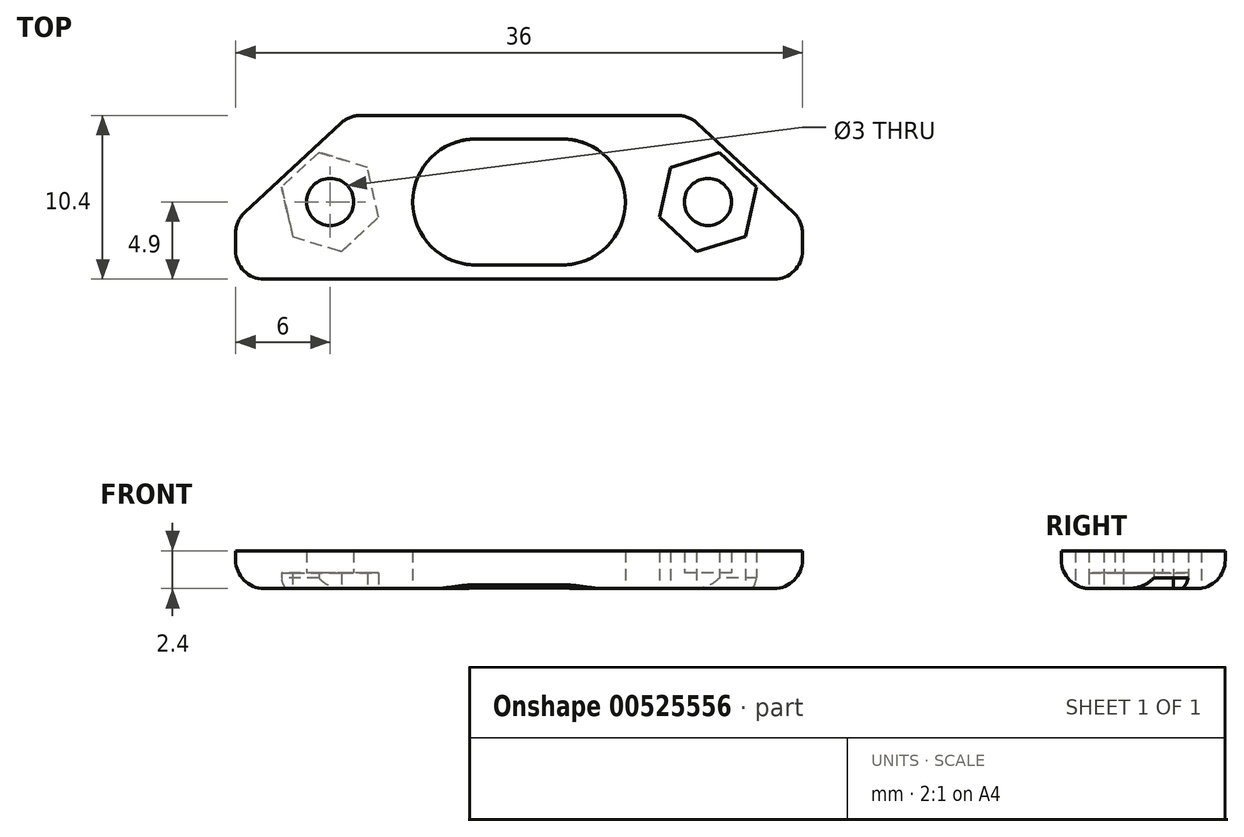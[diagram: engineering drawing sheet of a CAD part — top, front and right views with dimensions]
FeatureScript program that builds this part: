
annotation { "Feature Type Name" : "Feature", "Feature Type Description" : "" }
export const myFeature = defineFeature(function(context is Context, id is Id, definition is map)
    precondition{}
    {
        {
            var Q0;
            Q0=qCreatedBy(makeId("Top.planeOp"),FACE);
            var sketch = newSketch(context, id + "F0", { "sketchPlane" : qUnion([Q0])});
            skLineSegment(sketch, "E0.bottom", {"start": v(-18, -4.9) * mm, "end": v(18, -4.9) * mm});
            skLineSegment(sketch, "E0.top", {"start": v(-10.78, 5.5) * mm, "end": v(10.78, 5.5) * mm});
            skLineSegment(sketch, "E0.left", {"start": v(-18, -4.9) * mm, "end": v(-18, -1.2) * mm});
            skLineSegment(sketch, "E0.right", {"start": v(18, -4.9) * mm, "end": v(18, -1.2) * mm});
            skCircle(sketch, "E1", {"center": v(-12, 0) * mm, "radius": 1.5 * mm});
            skCircle(sketch, "E2.MirrorC", {"center": v(12, 0) * mm, "radius": 1.5 * mm});
            skArc(sketch, "E3", {"start": v(-2.75, 4) * mm, "mid": v(-6.75, 0) * mm, "end": v(-2.75, -4) * mm});
            skArc(sketch, "E4", {"start": v(2.75, -4) * mm, "mid": v(6.75, 0) * mm, "end": v(2.75, 4) * mm});
            skLineSegment(sketch, "E5", {"start": v(-2.75, 4) * mm, "end": v(2.75, 4) * mm});
            skLineSegment(sketch, "E6", {"start": v(-2.75, -4) * mm, "end": v(2.75, -4) * mm});
            skLineSegment(sketch, "E7", {"start": v(18, -1.2) * mm, "end": v(10.78, 5.5) * mm});
            skLineSegment(sketch, "E8.MirrorCS", {"start": v(-18, -1.2) * mm, "end": v(-10.78, 5.5) * mm});
            skPoint(sketch, "E9.center.orphan", {"position": v(-15.26, 6.06) * mm});
            skCircle(sketch, "E10.cCircle", {"center": v(12, 0) * mm, "radius": 2.8 * mm, "construction": true});
            skLineSegment(sketch, "E10.0", {"start": v(12.72, 3.15) * mm, "end": v(15.09, 0.95) * mm});
            skLineSegment(sketch, "E10.1", {"start": v(15.09, 0.95) * mm, "end": v(14.37, -2.2) * mm});
            skLineSegment(sketch, "E10.2", {"start": v(14.37, -2.2) * mm, "end": v(11.28, -3.15) * mm});
            skLineSegment(sketch, "E10.3", {"start": v(11.28, -3.15) * mm, "end": v(8.91, -0.95) * mm});
            skLineSegment(sketch, "E10.4", {"start": v(8.91, -0.95) * mm, "end": v(9.63, 2.2) * mm});
            skLineSegment(sketch, "E10.5", {"start": v(9.63, 2.2) * mm, "end": v(12.72, 3.15) * mm});
            skPoint(sketch, "E10.0.midPoint", {"position": v(13.9, 2.05) * mm});
            skLineSegment(sketch, "E11.MirrorCS", {"start": v(-8.91, -0.95) * mm, "end": v(-9.63, 2.2) * mm});
            skLineSegment(sketch, "E12.MirrorCS", {"start": v(-9.63, 2.2) * mm, "end": v(-12.72, 3.15) * mm});
            skLineSegment(sketch, "E13.MirrorCS", {"start": v(-12.72, 3.15) * mm, "end": v(-15.09, 0.95) * mm});
            skLineSegment(sketch, "E14.MirrorCS", {"start": v(-15.09, 0.95) * mm, "end": v(-14.37, -2.2) * mm});
            skLineSegment(sketch, "E15.MirrorCS", {"start": v(-14.37, -2.2) * mm, "end": v(-11.28, -3.15) * mm});
            skLineSegment(sketch, "E16.MirrorCS", {"start": v(-11.28, -3.15) * mm, "end": v(-8.91, -0.95) * mm});
            skCircle(sketch, "E17.MirrorC", {"center": v(-12, 0) * mm, "radius": 2.8 * mm, "construction": true});
            skSolve(sketch);
        }
        {
            var Q0;
            Q0=qSketchRegion(id+"F0",true);
            var Q1;
            Q1=makeQuery(id+"F0.imprint","IMPRINT",FACE,{"disambiguationData":[TD([[makeQuery(id+"F0.imprint","IMPRINT",EDGE,{"derivedFrom":sQuery(id+"F0.wireOp",EDGE,"E1")}),-1.0]])]});
            var Q2;
            Q2=makeQuery(id+"F0.imprint","IMPRINT",FACE,{"disambiguationData":[TD([[makeQuery(id+"F0.imprint","IMPRINT",EDGE,{"derivedFrom":sQuery(id+"F0.wireOp",EDGE,"E2.MirrorC")}),1.0]])]});
            extrude(context, id + "F1", {"entities" : qUnion([Q0, Q1, Q2]), "depth" : 2.4 * mm, "offsetDistance" : 25 * mm});
        }
        {
            var Q0;
            Q0=makeQuery(id+"F0.imprint","IMPRINT",FACE,{"disambiguationData":[TD([[makeQuery(id+"F0.imprint","IMPRINT",EDGE,{"derivedFrom":sQuery(id+"F0.wireOp",EDGE,"E2.MirrorC")}),1.0]])]});
            var Q1;
            Q1=makeQuery(id+"F0.imprint","IMPRINT",FACE,{"disambiguationData":[TD([[makeQuery(id+"F0.imprint","IMPRINT",EDGE,{"derivedFrom":sQuery(id+"F0.wireOp",EDGE,"E1")}),-1.0]])]});
            extrude(context, id + "F2", {"entities" : qUnion([Q0, Q1]), "operationType" : NewBodyOperationType.REMOVE, "depth" : 1 * mm, "offsetDistance" : 25 * mm});
        }
        {
            var Q0;
            Q0=makeQuery(id+"F1.opExtrude","CAP_EDGE",EDGE,{"disambiguationData":[OSD([sQuery(id+"F0.wireOp",EDGE,"E0.left")])],"isStart":true});
            var Q1;
            Q1=makeQuery(id+"F1.opExtrude","CAP_EDGE",EDGE,{"disambiguationData":[OSD([sQuery(id+"F0.wireOp",EDGE,"E0.bottom")])],"isStart":true});
            var Q2;
            Q2=makeQuery(id+"F1.opExtrude","CAP_EDGE",EDGE,{"disambiguationData":[OSD([sQuery(id+"F0.wireOp",EDGE,"E0.right")])],"isStart":true});
            var Q3;
            Q3=makeQuery(id+"F1.opExtrude","CAP_EDGE",EDGE,{"disambiguationData":[OSD([sQuery(id+"F0.wireOp",EDGE,"E0.top")])],"isStart":true});
            var Q4;
            Q4=makeQuery(id+"F1.opExtrude","SWEPT_EDGE",EDGE,{"disambiguationData":[OSD([sQuery(id+"F0.wireOp",EDGE,"E0.top"),sQuery(id+"F0.wireOp",EDGE,"E7")])]});
            var Q5;
            Q5=makeQuery(id+"F1.opExtrude","CAP_EDGE",EDGE,{"disambiguationData":[OSD([sQuery(id+"F0.wireOp",EDGE,"E8.MirrorCS")])],"isStart":true});
            var Q6;
            Q6=makeQuery(id+"F1.opExtrude","CAP_EDGE",EDGE,{"disambiguationData":[OSD([sQuery(id+"F0.wireOp",EDGE,"E7")])],"isStart":true});
            var Q7;
            Q7=makeQuery(id+"F1.opExtrude","SWEPT_EDGE",EDGE,{"disambiguationData":[OSD([sQuery(id+"F0.wireOp",EDGE,"E0.bottom"),sQuery(id+"F0.wireOp",EDGE,"E0.left")])]});
            var Q8;
            Q8=makeQuery(id+"F1.opExtrude","SWEPT_EDGE",EDGE,{"disambiguationData":[OSD([sQuery(id+"F0.wireOp",EDGE,"E0.bottom"),sQuery(id+"F0.wireOp",EDGE,"E0.right")])]});
            var Q9;
            Q9=makeQuery(id+"F1.opExtrude","SWEPT_EDGE",EDGE,{"disambiguationData":[OSD([sQuery(id+"F0.wireOp",EDGE,"E0.left"),sQuery(id+"F0.wireOp",EDGE,"E8.MirrorCS")])]});
            var Q10;
            Q10=makeQuery(id+"F1.opExtrude","SWEPT_EDGE",EDGE,{"disambiguationData":[OSD([sQuery(id+"F0.wireOp",EDGE,"E0.right"),sQuery(id+"F0.wireOp",EDGE,"E7")])]});
            var Q11;
            Q11=makeQuery(id+"F1.opExtrude","SWEPT_EDGE",EDGE,{"disambiguationData":[OSD([sQuery(id+"F0.wireOp",EDGE,"E0.top"),sQuery(id+"F0.wireOp",EDGE,"E8.MirrorCS")])]});
            fillet(context, id + "F3", {"entities" : qUnion([Q0, Q1, Q2, Q3, Q4, Q5, Q6, Q7, Q8, Q9, Q10, Q11]), "radius" : 1.8 * mm, "tangentPropagation" : true, "allowEdgeOverflow" : false});
        }
    });
